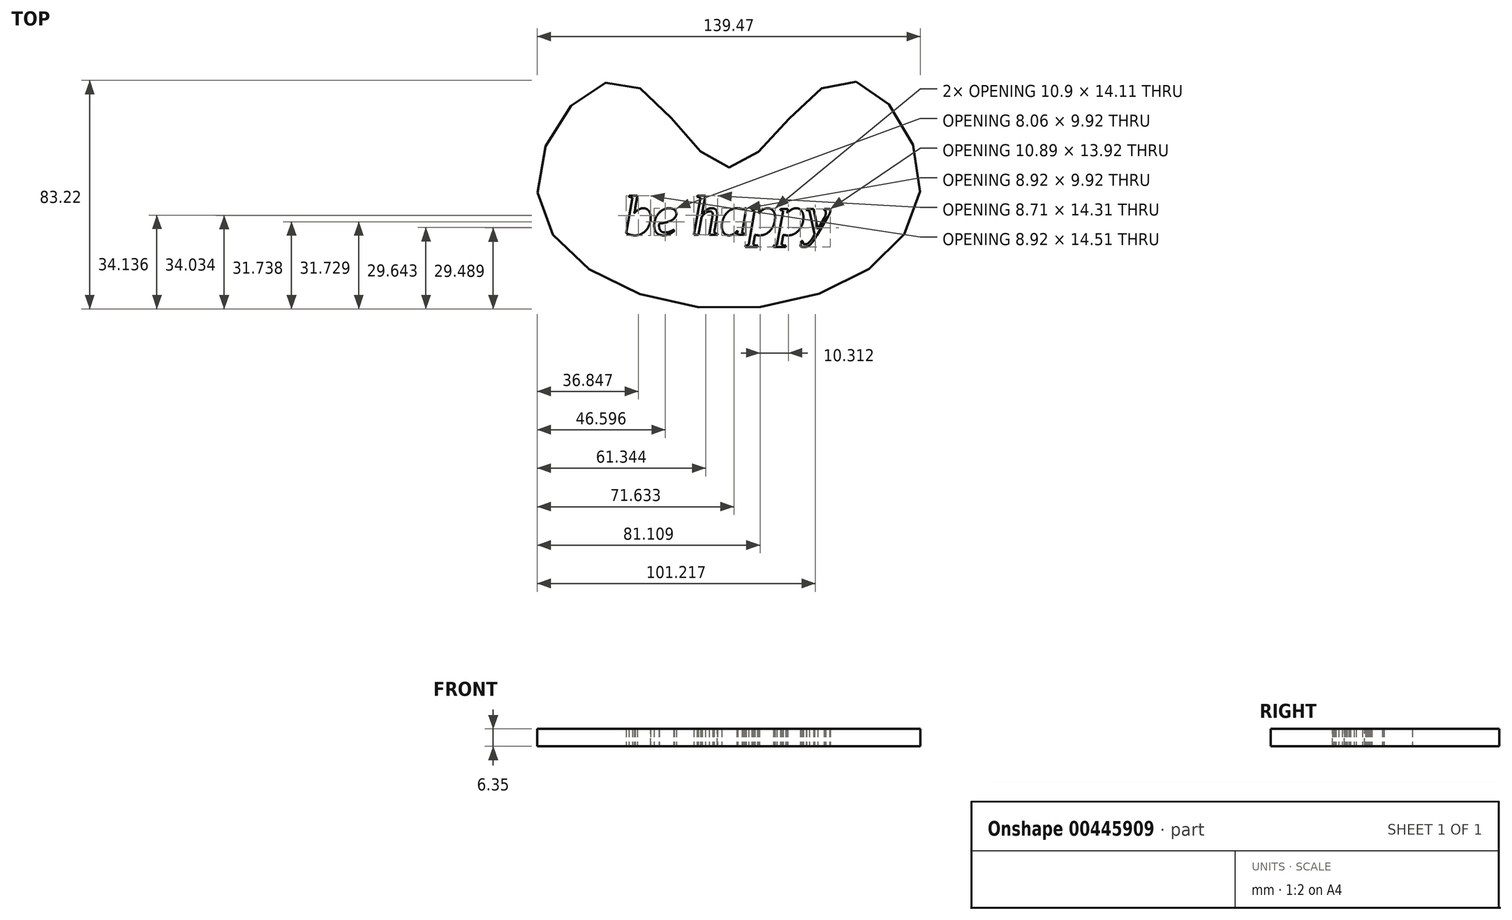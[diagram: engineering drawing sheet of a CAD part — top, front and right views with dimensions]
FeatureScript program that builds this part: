
annotation { "Feature Type Name" : "Feature", "Feature Type Description" : "" }
export const myFeature = defineFeature(function(context is Context, id is Id, definition is map)
    precondition{}
    {
        {
            var Q0;
            Q0=qCreatedBy(makeId("Top.planeOp"),FACE);
            var sketch = newSketch(context, id + "F0", { "sketchPlane" : qUnion([Q0])});
            skText(sketch, "E0", { "text": "be happy", "fontName": "Tinos-Italic.ttf"});
            skFitSpline(sketch, "E1", {"points": [v(38.17, 24.55) * mm, v(78.54, 56.08) * mm, v(107.64, 14.85) * mm, v(38.17, -26.98) * mm, v(-31.5, 14.85) * mm, v(0, 55.78) * mm, v(38.17, 24.55) * mm]});
            const initialGuessF0  = {"E0": [0, 0, 1, 0, 0.01485]};
            skSetInitialGuess(sketch, initialGuessF0);
            skSolve(sketch);
        }
        {
            var Q0;
            Q0=makeQuery(id+"F0.imprint","IMPRINT",FACE,{"disambiguationData":[TD([[makeQuery(id+"F0.imprint","IMPRINT",EDGE,{"derivedFrom":sQuery(id+"F0.wireOp",EDGE,"E0.sketch_text.stroke-0")}),1.0]])]});
            extrude(context, id + "F1", {"entities" : qUnion([Q0]), "depth" : 6.35 * mm});
        }
    });
